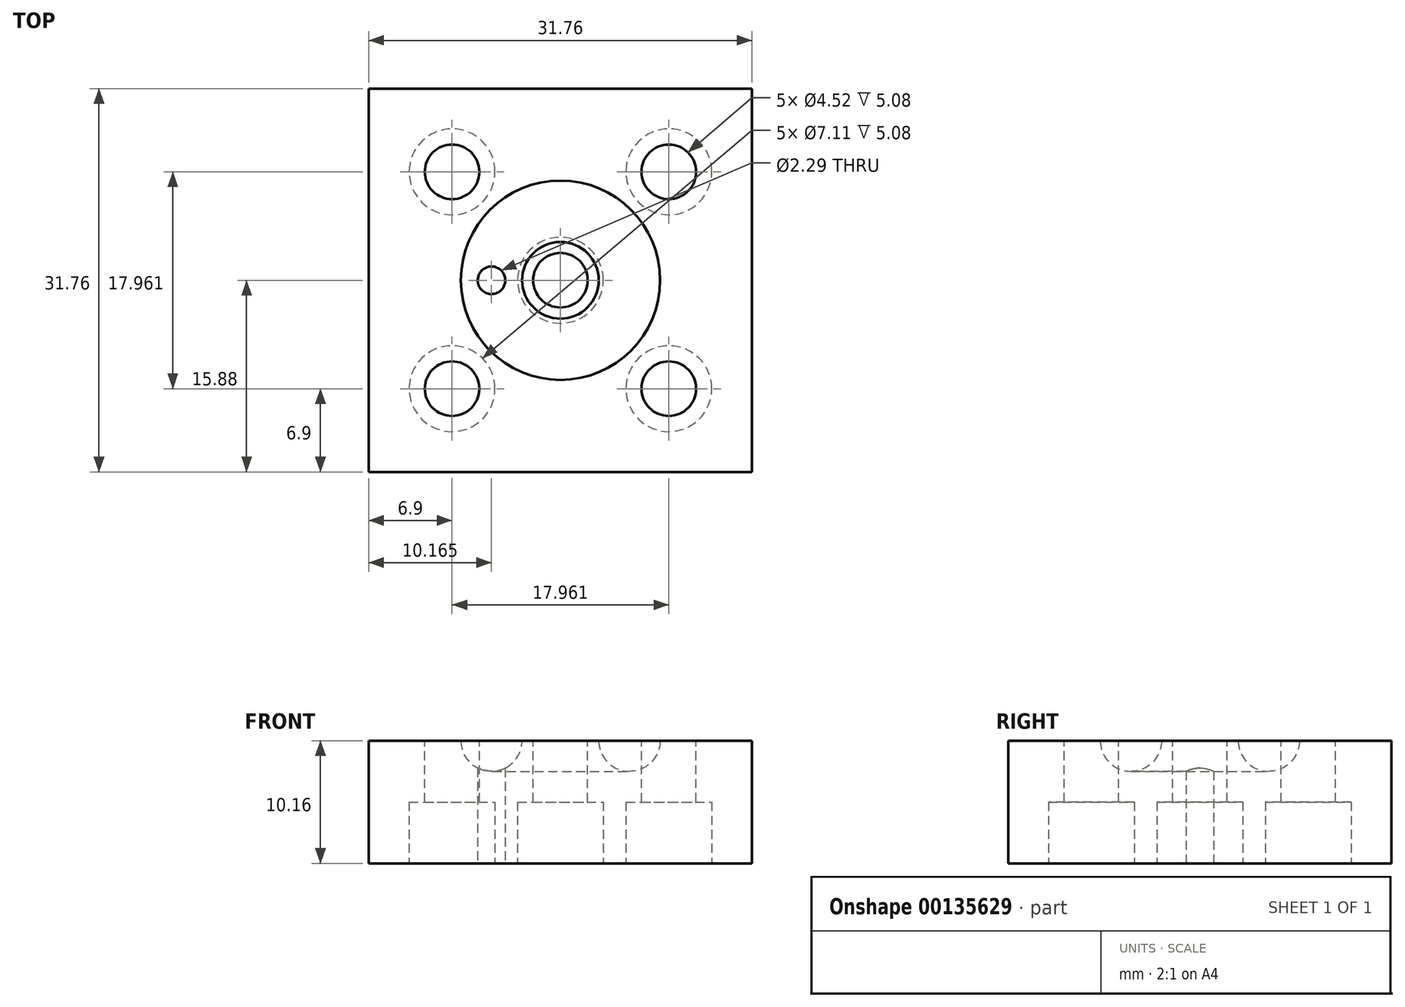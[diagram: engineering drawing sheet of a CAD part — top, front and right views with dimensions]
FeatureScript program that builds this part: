
annotation { "Feature Type Name" : "Feature", "Feature Type Description" : "" }
export const myFeature = defineFeature(function(context is Context, id is Id, definition is map)
    precondition{}
    {
        {
            var Q0;
            Q0=qCreatedBy(makeId("Top.planeOp"),FACE);
            var sketch = newSketch(context, id + "F0", { "sketchPlane" : qUnion([Q0])});
            skLineSegment(sketch, "E0.bottom", {"start": v(15.87, -15.87) * mm, "end": v(-15.88, -15.88) * mm});
            skLineSegment(sketch, "E0.top", {"start": v(15.87, 15.88) * mm, "end": v(-15.88, 15.88) * mm});
            skLineSegment(sketch, "E0.left", {"start": v(15.87, -15.88) * mm, "end": v(15.87, 15.88) * mm});
            skLineSegment(sketch, "E0.right", {"start": v(-15.88, -15.88) * mm, "end": v(-15.88, 15.88) * mm});
            skPoint(sketch, "E0.middle", {"position": v(0, 0) * mm});
            skSolve(sketch);
        }
        {
            var Q0;
            Q0=makeQuery(id+"F0.imprint","IMPRINT",FACE,{"disambiguationData":[TD([[makeQuery(id+"F0.imprint","IMPRINT",EDGE,{"derivedFrom":sQuery(id+"F0.wireOp",EDGE,"E0.bottom")}),-1.0]])]});
            extrude(context, id + "F1", {"entities" : qUnion([Q0]), "depth" : 10.16 * mm});
        }
        {
            var Q0;
            Q0=qCreatedBy(makeId("Front.planeOp"),FACE);
            var sketch = newSketch(context, id + "F2", { "sketchPlane" : qUnion([Q0])});
            skCircle(sketch, "E1", {"center": v(5.72, 10.16) * mm, "radius": 2.54 * mm});
            skLineSegment(sketch, "E2", {"start": v(0, 16.12) * mm, "end": v(0, 0) * mm, "construction": true});
            skSolve(sketch);
        }
        {
            var Q0;
            Q0=makeQuery(id+"F2.imprint","IMPRINT",FACE,{"disambiguationData":[TD([[makeQuery(id+"F2.imprint","IMPRINT",EDGE,{"derivedFrom":sQuery(id+"F2.wireOp",EDGE,"E1")}),1.0]])]});
            var Q1;
            Q1=sQuery(id+"F2.wireOp",EDGE,"E2");
            revolve(context, id + "F3", {"operationType" : NewBodyOperationType.REMOVE, "entities" : qUnion([Q0]), "axis" : qUnion([Q1]), "revolveType" : RevolveType.FULL, "oppositeDirection" : true});
        }
        {
            var Q0;
            {var subQ0=sQuery(id+"F0.wireOp",EDGE,"E0.right");var subQ1=sQuery(id+"F0.wireOp",EDGE,"E0.left");var subQ2=sQuery(id+"F0.wireOp",EDGE,"E0.top");var subQ3=sQuery(id+"F0.wireOp",EDGE,"E0.bottom");Q0=makeQuery(id+"F3.boolean.opBoolean","SPLIT",FACE,{"disambiguationData":[TD([makeQuery(id+"F1.opExtrude","SWEPT_FACE",FACE,{"disambiguationData":[OSD([subQ3])]}),makeQuery(id+"F1.opExtrude","SWEPT_FACE",FACE,{"disambiguationData":[OSD([subQ2])]}),makeQuery(id+"F1.opExtrude","SWEPT_FACE",FACE,{"disambiguationData":[OSD([subQ1])]}),makeQuery(id+"F1.opExtrude","SWEPT_FACE",FACE,{"disambiguationData":[OSD([subQ0])]}),makeQuery(id+"F3.opRevolve","SWEPT_FACE",FACE,{"disambiguationData":[OSD([sQuery(id+"F2.wireOp",EDGE,"E1")])]})])],"derivedFrom":makeQuery(id+"F1.opExtrude","CAP_FACE",FACE,{"disambiguationData":[OSD([subQ3,subQ2,subQ1,subQ0])],"isStart":false})});}
            var sketch = newSketch(context, id + "F4", { "sketchPlane" : qUnion([Q0])});
            skLineSegment(sketch, "E3", {"start": v(-15.88, 15.88) * mm, "end": v(15.88, -15.88) * mm, "construction": true});
            skLineSegment(sketch, "E4", {"start": v(15.88, 15.88) * mm, "end": v(-15.88, -15.88) * mm, "construction": true});
            skCircle(sketch, "E5", {"center": v(0, 0) * mm, "radius": 2.26 * mm});
            skCircle(sketch, "E6", {"center": v(-8.98, 8.98) * mm, "radius": 2.26 * mm});
            skLineSegment(sketch, "E7", {"start": v(0, 15.88) * mm, "end": v(0, -15.88) * mm, "construction": true});
            skLineSegment(sketch, "E8", {"start": v(-15.88, 0) * mm, "end": v(15.88, 0) * mm, "construction": true});
            skCircle(sketch, "E9.MirrorC", {"center": v(8.98, 8.98) * mm, "radius": 2.26 * mm});
            skCircle(sketch, "E10.MirrorC", {"center": v(-8.98, -8.98) * mm, "radius": 2.26 * mm});
            skCircle(sketch, "E11.MirrorC", {"center": v(8.98, -8.98) * mm, "radius": 2.26 * mm});
            skSolve(sketch);
        }
        {
            var Q0;
            Q0=qSketchRegion(id+"F4",true);
            extrude(context, id + "F5", {"entities" : qUnion([Q0]), "operationType" : NewBodyOperationType.REMOVE, "oppositeDirection" : true, "depth" : 25.4 * mm});
        }
        {
            var Q0;
            Q0=makeQuery(id+"F1.opExtrude","CAP_FACE",FACE,{"disambiguationData":[OSD([sQuery(id+"F0.wireOp",EDGE,"E0.bottom"),sQuery(id+"F0.wireOp",EDGE,"E0.top"),sQuery(id+"F0.wireOp",EDGE,"E0.left"),sQuery(id+"F0.wireOp",EDGE,"E0.right")])],"isStart":true});
            var sketch = newSketch(context, id + "F6", { "sketchPlane" : qUnion([Q0])});
            skCircle(sketch, "E12", {"center": v(0, 0) * mm, "radius": 3.56 * mm});
            skCircle(sketch, "E13", {"center": v(-8.98, 8.98) * mm, "radius": 3.56 * mm});
            skCircle(sketch, "E14.MirrorC", {"center": v(8.98, 8.98) * mm, "radius": 3.56 * mm});
            skCircle(sketch, "E15.MirrorC", {"center": v(-8.98, -8.98) * mm, "radius": 3.56 * mm});
            skCircle(sketch, "E16.MirrorC", {"center": v(8.98, -8.98) * mm, "radius": 3.56 * mm});
            skSolve(sketch);
        }
        {
            var Q0;
            Q0=qSketchRegion(id+"F6",true);
            extrude(context, id + "F7", {"entities" : qUnion([Q0]), "operationType" : NewBodyOperationType.REMOVE, "oppositeDirection" : true, "depth" : 5.08 * mm});
        }
        {
            var Q0;
            Q0=makeQuery(id+"F1.opExtrude","CAP_FACE",FACE,{"disambiguationData":[OSD([sQuery(id+"F0.wireOp",EDGE,"E0.bottom"),sQuery(id+"F0.wireOp",EDGE,"E0.top"),sQuery(id+"F0.wireOp",EDGE,"E0.left"),sQuery(id+"F0.wireOp",EDGE,"E0.right")])],"isStart":true});
            var sketch = newSketch(context, id + "F8", { "sketchPlane" : qUnion([Q0])});
            skCircle(sketch, "E17", {"center": v(-5.72, 0) * mm, "radius": 1.14 * mm});
            skSolve(sketch);
        }
        {
            var Q0;
            Q0 = qSketchRegion(id + "F8", true);
            extrude(context, id + "F9", {"entities" : qUnion([Q0]), "operationType" : NewBodyOperationType.REMOVE, "oppositeDirection" : true, "depth" : 25.4 * mm});
        }
    });
